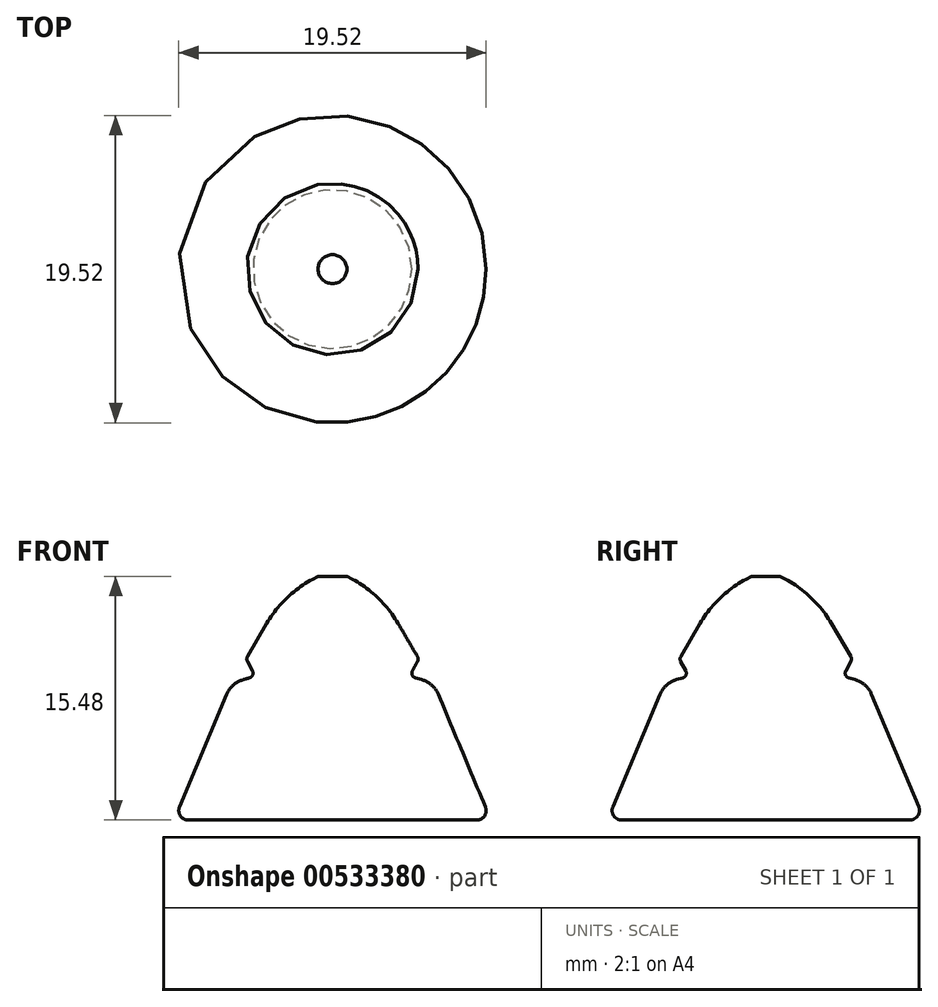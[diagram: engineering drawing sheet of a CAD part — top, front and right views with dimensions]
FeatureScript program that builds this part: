
annotation { "Feature Type Name" : "Feature", "Feature Type Description" : "" }
export const myFeature = defineFeature(function(context is Context, id is Id, definition is map)
    precondition{}
    {
        {
            var Q0;
            Q0=qCreatedBy(makeId("Front.planeOp"),FACE);
            var sketch = newSketch(context, id + "F0", { "sketchPlane" : qUnion([Q0])});
            skLineSegment(sketch, "E0", {"start": v(0, 0) * mm, "end": v(-10.06, 0) * mm});
            skLineSegment(sketch, "E1", {"start": v(-10.06, 0) * mm, "end": v(-6.42, 8.7) * mm});
            skLineSegment(sketch, "E2", {"start": v(-6.42, 8.7) * mm, "end": v(-4.9, 9.13) * mm});
            skLineSegment(sketch, "E3", {"start": v(-4.9, 9.13) * mm, "end": v(-5.49, 10.23) * mm});
            skLineSegment(sketch, "E4", {"start": v(-5.49, 10.23) * mm, "end": v(-3.12, 14.3) * mm});
            skLineSegment(sketch, "E5", {"start": v(-3.12, 14.3) * mm, "end": v(-0.92, 15.48) * mm});
            skLineSegment(sketch, "E6", {"start": v(-0.92, 15.48) * mm, "end": v(0, 15.48) * mm});
            skLineSegment(sketch, "E7", {"start": v(0, 15.48) * mm, "end": v(0, 0) * mm});
            skSolve(sketch);
        }
        {
            var Q0;
            Q0=makeQuery(id+"F0.imprint","IMPRINT",FACE,{"disambiguationData":[TD([[makeQuery(id+"F0.imprint","IMPRINT",EDGE,{"derivedFrom":sQuery(id+"F0.wireOp",EDGE,"E0")}),-1.0]])]});
            var Q1;
            Q1=sQuery(id+"F0.wireOp",EDGE,"E7");
            revolve(context, id + "F1", {"entities" : qUnion([Q0]), "axis" : qUnion([Q1]), "revolveType" : RevolveType.FULL});
        }
        {
            var Q0;
            Q0=makeQuery(id+"F1.opRevolve","SWEPT_FACE",FACE,{"disambiguationData":[OSD([sQuery(id+"F0.wireOp",EDGE,"E3")])]});
            fillet(context, id + "F2", {"entities" : qUnion([Q0]), "radius" : 0.32 * mm, "tangentPropagation" : true, "allowEdgeOverflow" : false});
        }
        {
            var Q0;
            Q0=makeQuery(id+"F1.opRevolve","SWEPT_EDGE",EDGE,{"disambiguationData":[OSD([sQuery(id+"F0.wireOp",EDGE,"E1"),sQuery(id+"F0.wireOp",EDGE,"E2")])]});
            fillet(context, id + "F3", {"entities" : qUnion([Q0]), "radius" : 1.61 * mm, "tangentPropagation" : true, "allowEdgeOverflow" : false});
        }
        {
            var Q0;
            Q0=makeQuery(id+"F1.opRevolve","SWEPT_EDGE",EDGE,{"disambiguationData":[OSD([sQuery(id+"F0.wireOp",EDGE,"E4"),sQuery(id+"F0.wireOp",EDGE,"E5")])]});
            fillet(context, id + "F4", {"entities" : qUnion([Q0]), "radius" : 7.46 * mm, "tangentPropagation" : true, "allowEdgeOverflow" : false});
        }
        {
            var Q0;
            Q0=makeQuery(id+"F1.opRevolve","SWEPT_EDGE",EDGE,{"disambiguationData":[OSD([sQuery(id+"F0.wireOp",EDGE,"E0"),sQuery(id+"F0.wireOp",EDGE,"E1")])]});
            fillet(context, id + "F5", {"entities" : qUnion([Q0]), "radius" : 0.6 * mm, "tangentPropagation" : true, "allowEdgeOverflow" : false});
        }
    });
